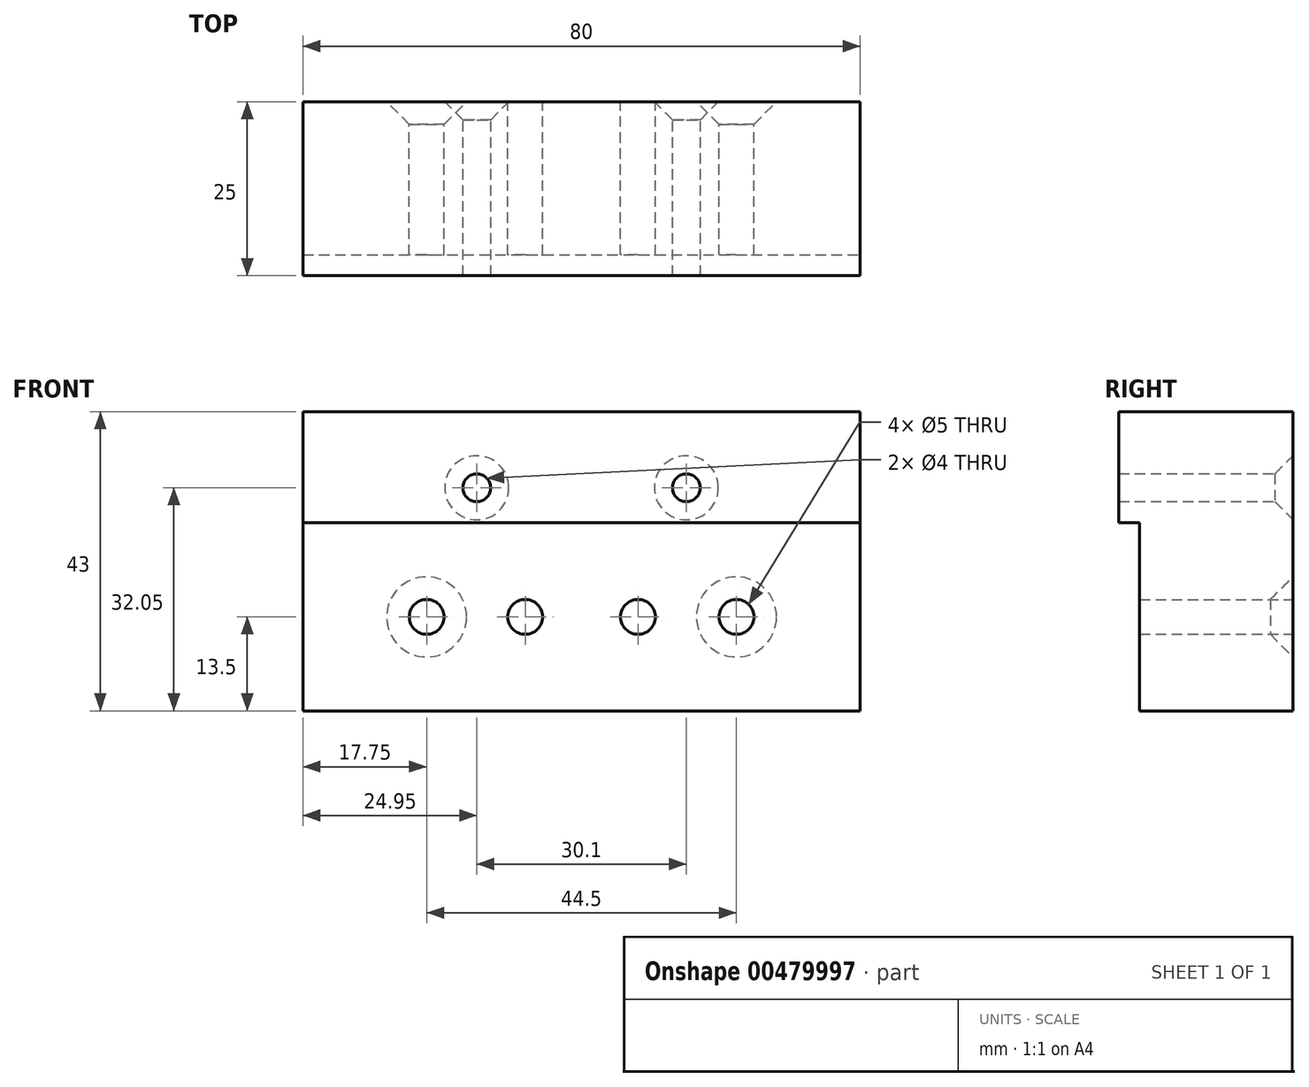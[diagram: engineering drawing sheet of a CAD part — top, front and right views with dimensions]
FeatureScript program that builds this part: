
annotation { "Feature Type Name" : "Feature", "Feature Type Description" : "" }
export const myFeature = defineFeature(function(context is Context, id is Id, definition is map)
    precondition{}
    {
        {
            var Q0;
            Q0=qCreatedBy(makeId("Front.planeOp"),FACE);
            var sketch = newSketch(context, id + "F0", { "sketchPlane" : qUnion([Q0])});
            skLineSegment(sketch, "E0.bottom", {"start": v(40, -21.5) * mm, "end": v(-40, -21.5) * mm});
            skLineSegment(sketch, "E0.top", {"start": v(40, 21.5) * mm, "end": v(-40, 21.5) * mm});
            skLineSegment(sketch, "E0.left", {"start": v(40, -21.5) * mm, "end": v(40, 21.5) * mm});
            skLineSegment(sketch, "E0.right", {"start": v(-40, -21.5) * mm, "end": v(-40, 21.5) * mm});
            skPoint(sketch, "E0.middle", {"position": v(0, 0) * mm});
            skSolve(sketch);
        }
        {
            var Q0;
            Q0=makeQuery(id+"F0.imprint","IMPRINT",FACE,{"disambiguationData":[TD([[makeQuery(id+"F0.imprint","IMPRINT",EDGE,{"derivedFrom":sQuery(id+"F0.wireOp",EDGE,"E0.bottom")}),-1.0]])]});
            extrude(context, id + "F1", {"entities" : qUnion([Q0]), "depth" : 25 * mm});
        }
        {
            var Q0;
            Q0=makeQuery(id+"F1.opExtrude","SWEPT_FACE",FACE,{"disambiguationData":[OSD([sQuery(id+"F0.wireOp",EDGE,"E0.left")])]});
            var sketch = newSketch(context, id + "F2", { "sketchPlane" : qUnion([Q0])});
            skLineSegment(sketch, "E1", {"start": v(-25, 5.5) * mm, "end": v(-22, 5.5) * mm});
            skLineSegment(sketch, "E2", {"start": v(-22, 5.5) * mm, "end": v(-22, -21.5) * mm});
            skLineSegment(sketch, "E3", {"start": v(-22, -21.5) * mm, "end": v(-25, -21.5) * mm});
            skLineSegment(sketch, "E4", {"start": v(-25, -21.5) * mm, "end": v(-25, 5.5) * mm});
            skSolve(sketch);
        }
        {
            var Q0;
            Q0=makeQuery(id+"F2.imprint","IMPRINT",FACE,{"disambiguationData":[TD([[makeQuery(id+"F2.imprint","IMPRINT",EDGE,{"derivedFrom":sQuery(id+"F2.wireOp",EDGE,"E1")}),-1.0]])]});
            extrude(context, id + "F3", {"entities" : qUnion([Q0]), "operationType" : NewBodyOperationType.REMOVE, "endBound" : BoundingType.THROUGH_ALL, "oppositeDirection" : true, "depth" : 25 * mm});
        }
        {
            var Q0;
            Q0=makeQuery(id+"F1.opExtrude","CAP_FACE",FACE,{"disambiguationData":[OSD([sQuery(id+"F0.wireOp",EDGE,"E0.bottom"),sQuery(id+"F0.wireOp",EDGE,"E0.top"),sQuery(id+"F0.wireOp",EDGE,"E0.left"),sQuery(id+"F0.wireOp",EDGE,"E0.right")])],"isStart":true});
            var sketch = newSketch(context, id + "F4", { "sketchPlane" : qUnion([Q0])});
            skPoint(sketch, "E5", {"position": v(-15.05, 10.55) * mm});
            skPoint(sketch, "E6", {"position": v(15.05, 10.55) * mm});
            skPoint(sketch, "E7", {"position": v(-22.25, -8) * mm});
            skPoint(sketch, "E8", {"position": v(-8.1, -8) * mm});
            skPoint(sketch, "E9", {"position": v(8.1, -8) * mm});
            skPoint(sketch, "E10", {"position": v(22.25, -8) * mm});
            skLineSegment(sketch, "E11", {"start": v(0, 23.38) * mm, "end": v(0, -20.11) * mm, "construction": true});
            skCircle(sketch, "E12", {"center": v(-8.1, -8) * mm, "radius": 2.5 * mm});
            skCircle(sketch, "E13", {"center": v(8.1, -8) * mm, "radius": 2.5 * mm});
            skSolve(sketch);
        }
        {
            var Q0;
            Q0=makeQuery(id+"F4.imprint","IMPRINT",FACE,{"disambiguationData":[TD([[makeQuery(id+"F4.imprint","IMPRINT",EDGE,{"derivedFrom":sQuery(id+"F4.wireOp",EDGE,"E12")}),1.0]])]});
            var Q1;
            Q1=makeQuery(id+"F4.imprint","IMPRINT",FACE,{"disambiguationData":[TD([[makeQuery(id+"F4.imprint","IMPRINT",EDGE,{"derivedFrom":sQuery(id+"F4.wireOp",EDGE,"E13")}),1.0]])]});
            extrude(context, id + "F5", {"entities" : qUnion([Q0, Q1]), "operationType" : NewBodyOperationType.REMOVE, "endBound" : BoundingType.THROUGH_ALL, "oppositeDirection" : true, "depth" : 25 * mm});
        }
        {
            var Q0;
            Q0=sQuery(id+"F4.wireOp",VERTEX,"E5");
            var Q1;
            Q1=sQuery(id+"F4.wireOp",VERTEX,"E6");
            var Q2;
            Q2=makeQuery(id+"F1.opExtrude","SWEPT_BODY",BODY,{"disambiguationData":[OSD([sQuery(id+"F0.wireOp",EDGE,"E0.bottom"),sQuery(id+"F0.wireOp",EDGE,"E0.top"),sQuery(id+"F0.wireOp",EDGE,"E0.left"),sQuery(id+"F0.wireOp",EDGE,"E0.right")])]});
            hole(context, id + "F6", {"style" : HoleStyle.C_SINK, "endStyle" : HoleEndStyle.THROUGH, "standardTappedOrClearance" : lookupTablePath({ "standard" : "ISO", "size" : "4", "type" : "Drilled" }), "standardBlindInLast" : lookupTablePath({ "standard" : "ISO", "size" : "4", "type" : "Drilled" }), "holeDiameter" : 4 * mm, "cSinkDiameter" : 9.2 * mm, "cSinkAngle" : 90 * degree, "isTappedThrough" : true, "tappedDepth" : 12 * mm, "tapClearance" : 3, "locations" : qUnion([Q0, Q1]), "scope" : qUnion([Q2])});
        }
        {
            var Q0;
            Q0=sQuery(id+"F4.wireOp",VERTEX,"E7");
            var Q1;
            Q1=sQuery(id+"F4.wireOp",VERTEX,"E10");
            var Q2;
            Q2=makeQuery(id+"F1.opExtrude","SWEPT_BODY",BODY,{"disambiguationData":[OSD([sQuery(id+"F0.wireOp",EDGE,"E0.bottom"),sQuery(id+"F0.wireOp",EDGE,"E0.top"),sQuery(id+"F0.wireOp",EDGE,"E0.left"),sQuery(id+"F0.wireOp",EDGE,"E0.right")])]});
            hole(context, id + "F7", {"style" : HoleStyle.C_SINK, "endStyle" : HoleEndStyle.THROUGH, "standardTappedOrClearance" : lookupTablePath({ "standard" : "ISO", "size" : "5", "type" : "Drilled" }), "standardBlindInLast" : lookupTablePath({ "standard" : "ISO", "size" : "5", "type" : "Drilled" }), "holeDiameter" : 5 * mm, "cSinkDiameter" : 11.5 * mm, "cSinkAngle" : 90 * degree, "isTappedThrough" : true, "tappedDepth" : 12 * mm, "tapClearance" : 3, "locations" : qUnion([Q0, Q1]), "scope" : qUnion([Q2])});
        }
    });
